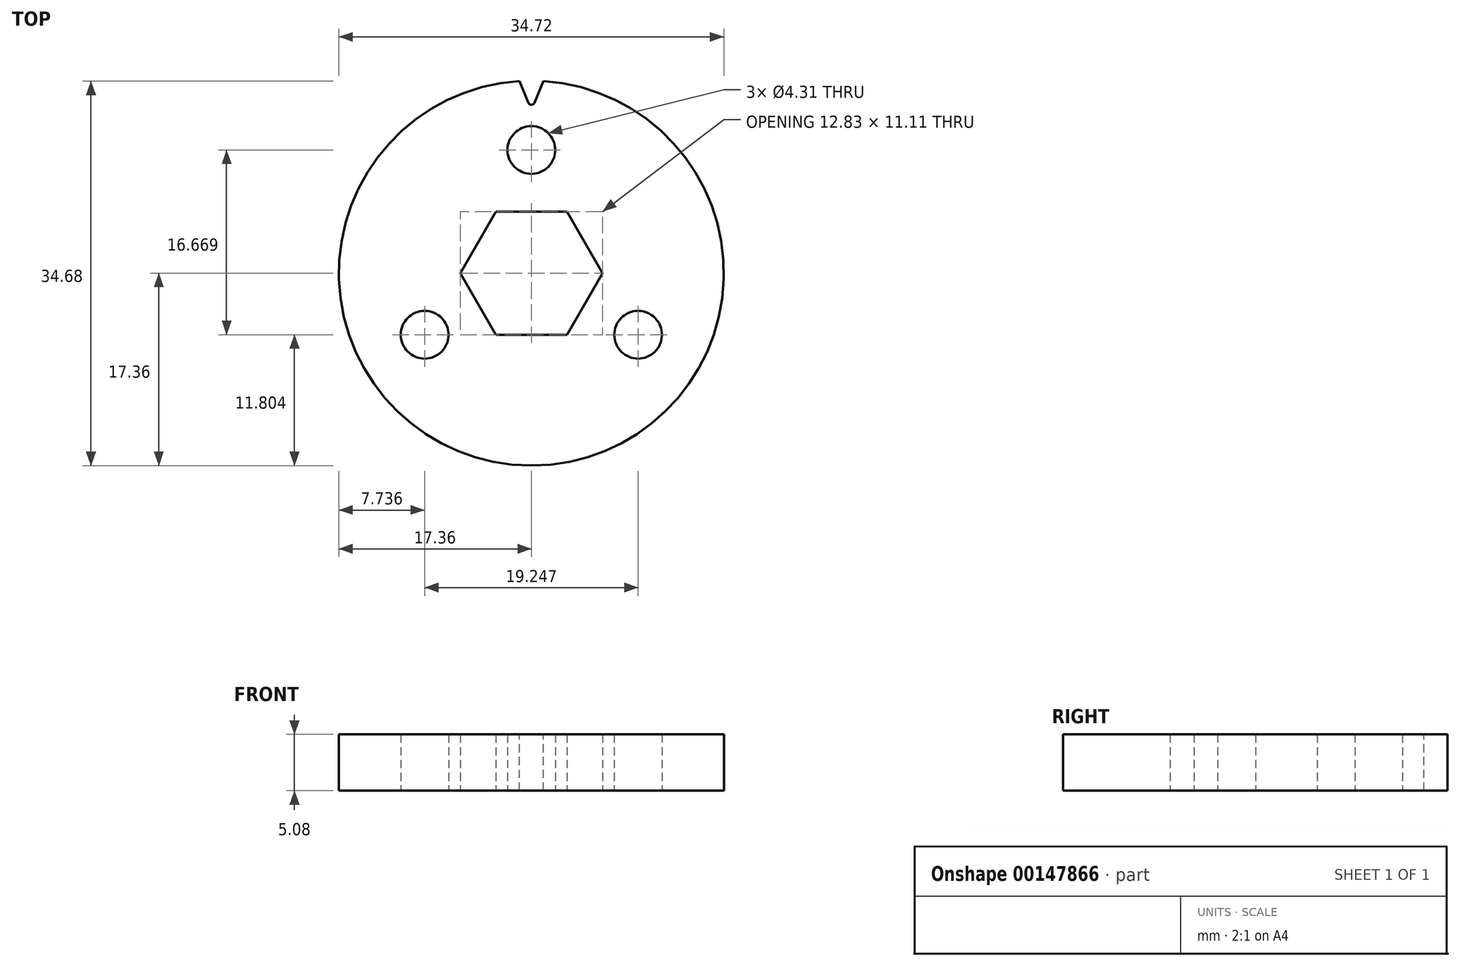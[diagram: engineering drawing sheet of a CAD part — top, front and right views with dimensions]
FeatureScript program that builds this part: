
annotation { "Feature Type Name" : "Feature", "Feature Type Description" : "" }
export const myFeature = defineFeature(function(context is Context, id is Id, definition is map)
    precondition{}
    {
        {
            var Q0;
            Q0=qCreatedBy(makeId("Top.planeOp"),FACE);
            var sketch = newSketch(context, id + "F0", { "sketchPlane" : qUnion([Q0])});
            skPoint(sketch, "E0.middle", {"position": v(0, 0) * mm});
            skCircle(sketch, "E1", {"center": v(0, 0) * mm, "radius": 17.36 * mm});
            skCircle(sketch, "E2.cCircle", {"center": v(0, 0) * mm, "radius": 5.56 * mm, "construction": true});
            skLineSegment(sketch, "E2.0", {"start": v(3.2, -5.56) * mm, "end": v(-3.2, -5.56) * mm});
            skLineSegment(sketch, "E2.1", {"start": v(-3.2, -5.56) * mm, "end": v(-6.42, 0) * mm});
            skLineSegment(sketch, "E2.2", {"start": v(-6.42, 0) * mm, "end": v(-3.2, 5.56) * mm});
            skLineSegment(sketch, "E2.3", {"start": v(-3.2, 5.56) * mm, "end": v(3.2, 5.56) * mm});
            skLineSegment(sketch, "E2.4", {"start": v(3.2, 5.56) * mm, "end": v(6.42, 0) * mm});
            skLineSegment(sketch, "E2.5", {"start": v(6.42, 0) * mm, "end": v(3.2, -5.56) * mm});
            skPoint(sketch, "E2.0.midPoint", {"position": v(0, -5.56) * mm});
            skCircle(sketch, "E3", {"center": v(0, 0) * mm, "radius": 7.14 * mm, "construction": true});
            skLineSegment(sketch, "E4.0", {"start": v(9.62, -5.56) * mm, "end": v(-9.62, -5.56) * mm, "construction": true});
            skLineSegment(sketch, "E4.1", {"start": v(-9.62, -5.56) * mm, "end": v(0, 11.11) * mm, "construction": true});
            skLineSegment(sketch, "E4.2", {"start": v(0, 11.11) * mm, "end": v(9.62, -5.56) * mm, "construction": true});
            skCircle(sketch, "E5", {"center": v(0, 11.11) * mm, "radius": 3.97 * mm, "construction": true});
            skCircle(sketch, "E6", {"center": v(0, 11.11) * mm, "radius": 2.15 * mm});
            skCircle(sketch, "E7", {"center": v(9.62, -5.56) * mm, "radius": 2.15 * mm});
            skCircle(sketch, "E8", {"center": v(-9.62, -5.56) * mm, "radius": 2.15 * mm});
            skSolve(sketch);
        }
        {
            var Q0;
            Q0=makeQuery(id+"F0.imprint","IMPRINT",FACE,{"disambiguationData":[TD([[makeQuery(id+"F0.imprint","IMPRINT",EDGE,{"derivedFrom":sQuery(id+"F0.wireOp",EDGE,"E0.left")}),1.0]])]});
            var Q1;
            Q1=makeQuery(id+"F0.imprint","IMPRINT",FACE,{"disambiguationData":[TD([[makeQuery(id+"F0.imprint","IMPRINT",EDGE,{"derivedFrom":sQuery(id+"F0.wireOp",EDGE,"E1")}),1.0]])]});
            extrude(context, id + "F1", {"entities" : qUnion([Q0, Q1]), "depth" : 5.08 * mm});
        }
        {
            var Q0;
            Q0=makeQuery(id+"F1.opExtrude","CAP_FACE",FACE,{"disambiguationData":[OSD([sQuery(id+"F0.wireOp",EDGE,"E0.left"),sQuery(id+"F0.wireOp",EDGE,"E0.right"),sQuery(id+"F0.wireOp",EDGE,"ScfBMfkV-s1yN-Ls9R-SGr5-fEyGpD6zak8e"),sQuery(id+"F0.wireOp",EDGE,"xnxmVwjl-FvSF-m7sj-be2U-u85gZZGoORGZ"),sQuery(id+"F0.wireOp",EDGE,"E1")])],"isStart":false});
            var sketch = newSketch(context, id + "F2", { "sketchPlane" : qUnion([Q0])});
            skLineSegment(sketch, "E9", {"start": v(0, 0) * mm, "end": v(0, 17.36) * mm, "construction": true});
            skLineSegment(sketch, "E10", {"start": v(0, 0) * mm, "end": v(0.72, 17.34) * mm, "construction": true});
            skArc(sketch, "E11", {"start": v(1.08, 17.32) * mm, "mid": v(0, 17.36) * mm, "end": v(-1.08, 17.32) * mm});
            skLineSegment(sketch, "E12", {"start": v(-1.08, 17.32) * mm, "end": v(-0.28, 15.38) * mm});
            skLineSegment(sketch, "E13", {"start": v(1.08, 17.32) * mm, "end": v(0.28, 15.38) * mm});
            skPoint(sketch, "E14", {"position": v(0.68, 16.35) * mm});
            skArc(sketch, "E15", {"start": v(-0.28, 15.38) * mm, "mid": v(0, 15.2) * mm, "end": v(0.28, 15.38) * mm});
            skSolve(sketch);
        }
        {
            var Q0;
            Q0=qSketchRegion(id+"F2",true);
            var Q1;
            Q1=makeQuery(id+"F1.opExtrude","CAP_FACE",FACE,{"disambiguationData":[OSD([sQuery(id+"F0.wireOp",EDGE,"E0.left"),sQuery(id+"F0.wireOp",EDGE,"E0.right"),sQuery(id+"F0.wireOp",EDGE,"ScfBMfkV-s1yN-Ls9R-SGr5-fEyGpD6zak8e"),sQuery(id+"F0.wireOp",EDGE,"xnxmVwjl-FvSF-m7sj-be2U-u85gZZGoORGZ"),sQuery(id+"F0.wireOp",EDGE,"E1")])],"isStart":true});
            extrude(context, id + "F3", {"entities" : qUnion([Q0]), "operationType" : NewBodyOperationType.REMOVE, "endBound" : BoundingType.UP_TO_SURFACE, "oppositeDirection" : true, "endBoundEntityFace" : qUnion([Q1]), "depth" : 25.4 * mm});
        }
    });
